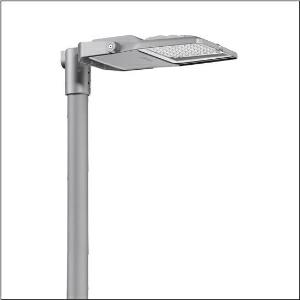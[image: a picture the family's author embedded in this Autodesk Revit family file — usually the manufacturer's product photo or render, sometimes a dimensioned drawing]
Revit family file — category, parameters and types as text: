
# Revit family: floodlight_fl_21_iq_mini___pl33t_5xa7772c4f3a_1e48
name_source: partatom
category: Lighting Fixtures
units: mm (PartAtom-declared; Revit-internal decimal feet)

## family parameters
Cut with Voids When Loaded = No
Host = Face
Light Source = No
Part Type = Normal
Room Calculation Point = No
Round Connector Dimension = Use Diameter
Shared = No

## types (1)
- --- (1 x LED, 12570 lm, 87.2 W, 4000K)
    Apparent Load = 87 VA
    CIE Flux Codes = 26 75 99 100 100
    Color Rendering = 70
    Color Temperature = 4000K
    Default Elevation = 1800 mm
    Description = Floodlight FL 21 iQ mini, floodlight, primary light control with lens, of PMMA, primary optical cover: protective disc, of toughened safety glass, transparent, light distribution: PL33T, light emission: direct distribution, installation type: surface-mounted, LED, High Power LED, rated luminous flux: 12.570lm, luminous efficacy: 144lm/W, light colour: 740, colour temperature: 4000K, control: Auto-Match, Temp-Guard, Night-Set, Smart-Wire, Desk-Remote (wireless, voltage-free reading and setting of iQ features in the workshop via application-optimized NFC function/RFID function), optimised constant luminous flux control (CLO 2.0), Light-Fading, Lumen-Switch, with terminal, 6-pole, mains connection: 220..240V, AC, 50/60Hz, start of lifetime: 87W, end of service life: 92W, reduction: 40W, luminaire housing, of diecast aluminium, powder-coated, Siteco® metallic grey (DB 702S), corrosivity category C5 mid according to DIN EN ISO 12944, sealing non-destructively replaceable, please order mast flange separately, mast bracket, of steel, galvanised, powder-coated, protection rating (complete): IP66, insulation class (complete): insulation class II (safety insulation), certification: CE, ENEC, VDE, protection symbol: D, impact resistance: IK08, permissible operating ambient temperature: -40..+40°C, permissible operating ambient temperature for outdoor applications: -40..+50°C, standard: DIN EN 12944, LABS conformity tested according to VDMA 24364:2018-05, packaging unit: 1 piece

Light Distribution: PL33T
    Height = 70 mm
    Lamp = 1 x LED
    Lamp Light Flux = 12570 lm
    Lamp Power = 87.2 W
    Lamp count = 1
    Length = 485 mm
    Luminous efficacy = 144 lm/W
    Manufacturer = Siteco
    ModVariant = No
    Model = 5XA7772C4F3A
    Number of Poles = 1
    OnlyDefault = Yes
    Power Factor = 1
    Product Name = Floodlight FL 21 iQ mini | PL33T
    Product group = floodlight | pylon annexe
    ProductGroupID = 6200
    Protection Class = Protection class II
    Protection Degree = IP 66
    RLX_Detail_Level = 1
    RLX_Emergency_Light_Flux = 0 lm
    RLX_Emergency_Type = 0
    RLX_Emergency_Type_DB = No
    RlxData = <blob elided: 101265 chars, md5=d5dfd23f>
    Socket = socket
    Standby Power = 0 W
    System Light Flux = 12570 lm
    System Power = 87 W
    Type Comments = factory setting: luminous flux: 100 % | dim-lin: 254 | 456 mA
    Type Image = l_1007125.jpg
    URL = http://relux.com
    VarID = @adj_081831
    Voltage = 0 V
    Weight = 0.00 kg
    Width = 337 mm

## geometry (parser evidence)
native form markers: Blend x4, Sweep x11
no freeform markers — native parametric forms only
